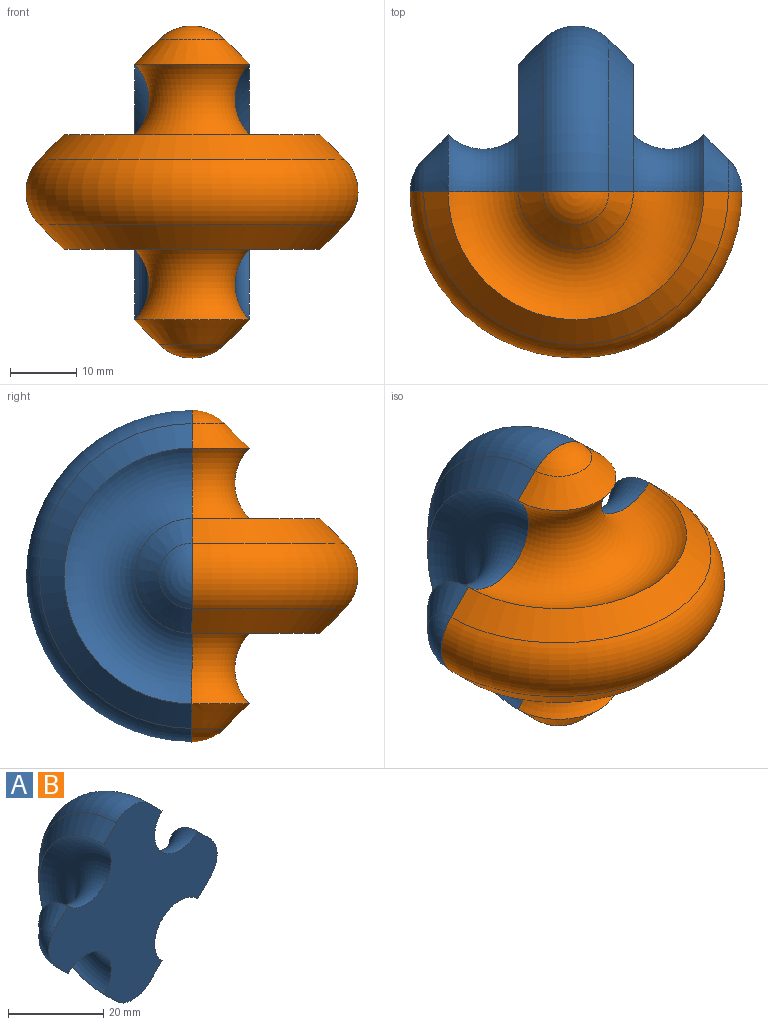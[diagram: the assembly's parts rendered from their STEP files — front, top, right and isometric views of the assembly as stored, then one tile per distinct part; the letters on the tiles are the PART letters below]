
ASSEMBLY  parts=2 mates=1
PART A: 10 faces, bbox 50x27.1x54.1 mm
  f0: torus R=13.95mm, axis (1,0,0), area 782.7mm2, adj f1,f7,f8
  f1: cone r=4.95mm half-angle=45deg, axis (1,0,0), area 111.7mm2, adj f0,f2,f8
  f2: sphere r=7mm, area 45.1mm2, adj f1,f8
  f3: sphere r=7mm, area 45.1mm2, adj f4,f8
  f4: cone r=4.95mm half-angle=45deg, axis (-1,0,0), area 111.7mm2, adj f3,f5,f8
  f5: torus R=13.95mm, axis (1,0,0), area 782.7mm2, adj f4,f6,f8
  f6: cone r=19.25mm half-angle=45deg, axis (-1,0,0), area 346.6mm2, adj f5,f8,f9
  f7: cone r=19.25mm half-angle=45deg, axis (1,0,0), area 346.6mm2, adj f0,f8,f9
  f8: plane 50x50mm, normal (0,-1,0), area 1161.3mm2, adj f0,f1,f2,f3,f4,f5,f6,f7
  f9: torus R=18mm, axis (-1,0,0), area 839.5mm2, adj f6,f7,f8
PART B: same geometry as A
PLACE A at identity fixed
PLACE B rot(axis=(0.71,0,0.71),180deg) t=(0,0,0)mm
MATE fastened A.f8 <-> B.f8  axis (0,-1,0) through (0,0,0)mm
